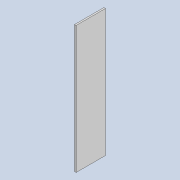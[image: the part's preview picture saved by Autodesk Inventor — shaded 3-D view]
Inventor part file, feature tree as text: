
AUTODESK INVENTOR PART (.ipt)
format: ipt  version: 2021 (Build 250183000, 183)  size: 80,384 bytes
history: native  units: mm
features: extrude x1, sketch x1
ambient origin geometry x8: Origin, YZ Plane, XZ Plane, XY Plane, X Axis, Y Axis, Z Axis, Center Point
bodies: Solid1 (feature_tree)
feature tree (2):
  extrude  "Extrusion1"  Depth=180.0mm
  sketch  "Sketch1"  dims[d0=780.0mm d1=180.0mm d2=10.0mm d3=0.0mm]
